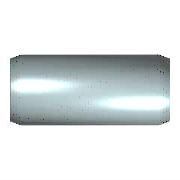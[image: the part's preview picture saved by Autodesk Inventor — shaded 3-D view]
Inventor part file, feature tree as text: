
AUTODESK INVENTOR PART (.ipt)
format: ipt  version: 2023.3 (Build 273359000, 359)  size: 116,736 bytes
history: native  units: mm (DEFAULTED — no unit token found)
features: extrude x1, chamfer x1, sketch x1
ambient origin geometry x8: Origin, YZ Plane, XZ Plane, XY Plane, X Axis, Y Axis, Z Axis, Center Point
bodies: Solid1 (feature_tree)
feature tree (3):
  extrude  "Körper"  Depth=8.0mm
  chamfer  "Skizze2"  [1 undecoded]
  sketch  "Skizze"  dims[d1=3.0mm d2=8.0mm d3=0.0mm d4=0.5mm d5=15.0deg d8=0.5mm d9=15.0deg d11=0.5mm d12=0.5mm d13=0.0mm d15=0.0mm d16=0.0mm]
note: 1 required parameter value undecoded (feature->parameter linkage not recoverable at this tier; creation-order binding heuristic only, values carry confidence <= 0.55)
